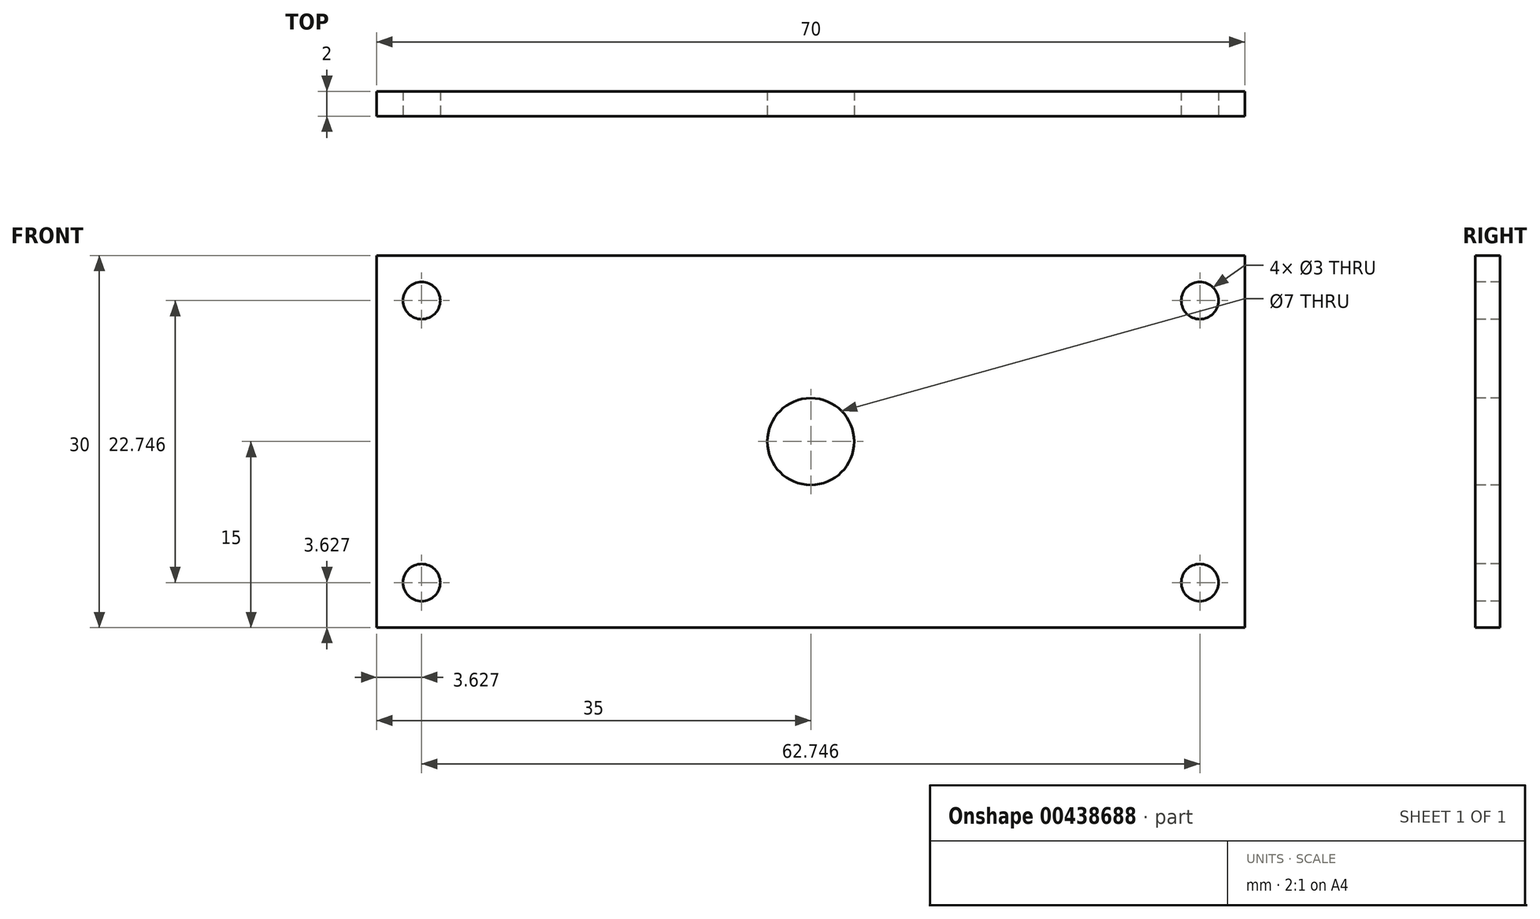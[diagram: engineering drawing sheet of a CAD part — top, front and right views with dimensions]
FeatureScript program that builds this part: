
annotation { "Feature Type Name" : "Feature", "Feature Type Description" : "" }
export const myFeature = defineFeature(function(context is Context, id is Id, definition is map)
    precondition{}
    {
        {
            var Q0;
            Q0=qCreatedBy(makeId("Front.planeOp"),FACE);
            var sketch = newSketch(context, id + "F0", { "sketchPlane" : qUnion([Q0])});
            skLineSegment(sketch, "E0.bottom", {"start": v(35, 15) * mm, "end": v(-35, 15) * mm});
            skLineSegment(sketch, "E0.top", {"start": v(35, -15) * mm, "end": v(-35, -15) * mm});
            skLineSegment(sketch, "E0.left", {"start": v(35, 15) * mm, "end": v(35, -15) * mm});
            skLineSegment(sketch, "E0.right", {"start": v(-35, 15) * mm, "end": v(-35, -15) * mm});
            skPoint(sketch, "E0.middle", {"position": v(0, 0) * mm});
            skSolve(sketch);
        }
        {
            var Q0;
            Q0 = qSketchRegion(id + "F0", true);
            extrude(context, id + "F1", {"entities" : qUnion([Q0]), "depth" : 2 * mm});
        }
        {
            var Q0;
            Q0=makeQuery(id+"F1.opExtrude","CAP_FACE",FACE,{"disambiguationData":[OSD([sQuery(id+"F0.wireOp",EDGE,"E0.bottom"),sQuery(id+"F0.wireOp",EDGE,"E0.top"),sQuery(id+"F0.wireOp",EDGE,"E0.left"),sQuery(id+"F0.wireOp",EDGE,"E0.right")])],"isStart":false});
            var sketch = newSketch(context, id + "F2", { "sketchPlane" : qUnion([Q0])});
            skLineSegment(sketch, "E1", {"start": v(-27.75, 7.75) * mm, "end": v(-35, 15) * mm, "construction": true});
            skCircle(sketch, "E2", {"center": v(-31.37, 11.37) * mm, "radius": 1.5 * mm});
            skCircle(sketch, "E3.MirrorC", {"center": v(31.37, 11.37) * mm, "radius": 1.5 * mm});
            skCircle(sketch, "E4.MirrorC", {"center": v(-31.37, -11.37) * mm, "radius": 1.5 * mm});
            skCircle(sketch, "E5.MirrorC", {"center": v(31.37, -11.37) * mm, "radius": 1.5 * mm});
            skSolve(sketch);
        }
        {
            var Q0;
            Q0 = qSketchRegion(id + "F2", true);
            extrude(context, id + "F3", {"entities" : qUnion([Q0]), "operationType" : NewBodyOperationType.REMOVE, "oppositeDirection" : true, "depth" : 25 * mm});
        }
        {
            var Q0;
            Q0=makeQuery(id+"F1.opExtrude","CAP_FACE",FACE,{"disambiguationData":[OSD([sQuery(id+"F0.wireOp",EDGE,"E0.bottom"),sQuery(id+"F0.wireOp",EDGE,"E0.top"),sQuery(id+"F0.wireOp",EDGE,"E0.left"),sQuery(id+"F0.wireOp",EDGE,"E0.right")])],"isStart":false});
            var sketch = newSketch(context, id + "F4", { "sketchPlane" : qUnion([Q0])});
            skCircle(sketch, "E6", {"center": v(0, 0) * mm, "radius": 3.5 * mm});
            skSolve(sketch);
        }
        {
            var Q0;
            Q0 = qSketchRegion(id + "F4", true);
            extrude(context, id + "F5", {"entities" : qUnion([Q0]), "operationType" : NewBodyOperationType.REMOVE, "endBound" : BoundingType.THROUGH_ALL, "oppositeDirection" : true, "depth" : 25 * mm});
        }
    });
